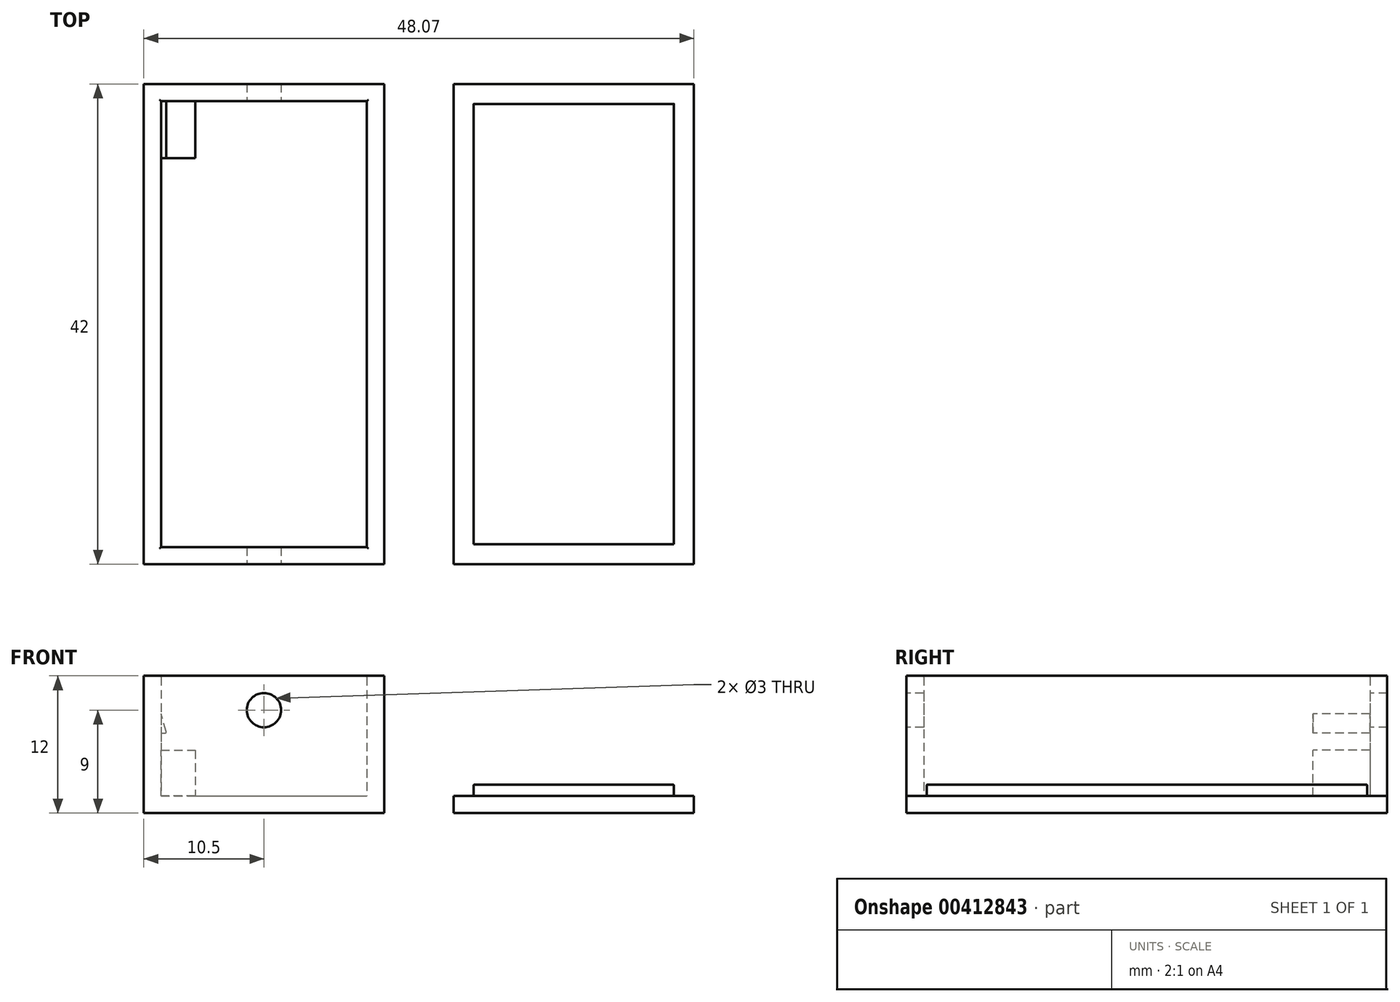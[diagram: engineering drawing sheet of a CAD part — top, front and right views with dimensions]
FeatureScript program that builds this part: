
annotation { "Feature Type Name" : "Feature", "Feature Type Description" : "" }
export const myFeature = defineFeature(function(context is Context, id is Id, definition is map)
    precondition{}
    {
        {
            var Q0;
            Q0=qCreatedBy(makeId("Top.planeOp"),FACE);
            var sketch = newSketch(context, id + "F0", { "sketchPlane" : qUnion([Q0])});
            skLineSegment(sketch, "E0.bottom", {"start": v(-10.5, 21) * mm, "end": v(10.5, 21) * mm});
            skLineSegment(sketch, "E0.top", {"start": v(-10.5, -21) * mm, "end": v(10.5, -21) * mm});
            skLineSegment(sketch, "E0.left", {"start": v(-10.5, 21) * mm, "end": v(-10.5, -21) * mm});
            skLineSegment(sketch, "E0.right", {"start": v(10.5, 21) * mm, "end": v(10.5, -21) * mm});
            skSolve(sketch);
        }
        {
            var Q0;
            Q0 = qSketchRegion(id + "F0", true);
            extrude(context, id + "F1", {"entities" : qUnion([Q0]), "depth" : 12 * mm});
        }
        {
            var Q0;
            Q0=makeQuery(id+"F1.opExtrude","CAP_FACE",FACE,{"disambiguationData":[OSD([sQuery(id+"F0.wireOp",EDGE,"E0.bottom"),sQuery(id+"F0.wireOp",EDGE,"E0.top"),sQuery(id+"F0.wireOp",EDGE,"E0.left"),sQuery(id+"F0.wireOp",EDGE,"E0.right")])],"isStart":false});
            shell(context, id + "F2", {"entities" : qUnion([Q0]), "thickness" : 1.5 * mm});
        }
        {
            var Q0;
            Q0=qCreatedBy(makeId("Top.planeOp"),FACE);
            var sketch = newSketch(context, id + "F3", { "sketchPlane" : qUnion([Q0])});
            skLineSegment(sketch, "E1.bottom", {"start": v(-10.5, 21) * mm, "end": v(-6, 21) * mm});
            skLineSegment(sketch, "E1.top", {"start": v(-10.5, 14.5) * mm, "end": v(-6, 14.5) * mm});
            skLineSegment(sketch, "E1.left", {"start": v(-10.5, 21) * mm, "end": v(-10.5, 14.5) * mm});
            skLineSegment(sketch, "E1.right", {"start": v(-6, 21) * mm, "end": v(-6, 14.5) * mm});
            skSolve(sketch);
        }
        {
            var Q0;
            Q0 = qSketchRegion(id + "F3", true);
            extrude(context, id + "F4", {"entities" : qUnion([Q0]), "operationType" : NewBodyOperationType.ADD, "depth" : (4 + 1.5) * mm});
        }
        {
            var Q0;
            Q0=makeQuery(id+"F4.opExtrude","CAP_FACE",FACE,{"disambiguationData":[OSD([sQuery(id+"F3.wireOp",EDGE,"E1.bottom"),sQuery(id+"F3.wireOp",EDGE,"E1.top"),sQuery(id+"F3.wireOp",EDGE,"E1.left"),sQuery(id+"F3.wireOp",EDGE,"E1.right")])],"isStart":false});
            cPlane(context, id + "F5", {"entities" : qUnion([Q0]), "cplaneType" : CPlaneType.OFFSET, "offset" : 1.5 * mm, "width" : 150 * mm, "height" : 150 * mm});
        }
        {
            var Q0;
            Q0=makeQuery(id+"F4.opExtrude","SWEPT_FACE",FACE,{"disambiguationData":[OSD([sQuery(id+"F3.wireOp",EDGE,"E1.top")])]});
            var sketch = newSketch(context, id + "F6", { "sketchPlane" : qUnion([Q0])});
            skLineSegment(sketch, "E2.0", {"start": v(-9, 12) * mm, "end": v(-9, 1.5) * mm, "construction": true});
            skLineSegment(sketch, "E3.0", {"start": v(-9, 5.5) * mm, "end": v(-6, 5.5) * mm, "construction": true});
            skLineSegment(sketch, "E4", {"start": v(-9, 7) * mm, "end": v(-8.5, 7) * mm});
            skLineSegment(sketch, "E5", {"start": v(-8.5, 7) * mm, "end": v(-9, 8.7) * mm});
            skLineSegment(sketch, "E6", {"start": v(-9, 8.7) * mm, "end": v(-9, 7) * mm});
            skSolve(sketch);
        }
        {
            var Q0;
            Q0 = qSketchRegion(id + "F6", true);
            extrude(context, id + "F7", {"entities" : qUnion([Q0]), "operationType" : NewBodyOperationType.ADD, "endBound" : BoundingType.UP_TO_NEXT, "oppositeDirection" : true, "depth" : 25 * mm});
        }
        {
            var Q0;
            Q0=makeQuery(id+"F1.opExtrude","SWEPT_FACE",FACE,{"disambiguationData":[OSD([sQuery(id+"F0.wireOp",EDGE,"E0.top")])]});
            var sketch = newSketch(context, id + "F8", { "sketchPlane" : qUnion([Q0])});
            skPoint(sketch, "E7", {"position": v(0, 9) * mm});
            skSolve(sketch);
        }
        {
            var Q0;
            Q0=sQuery(id+"F8.wireOp",VERTEX,"E7");
            var Q1;
            Q1=makeQuery(id+"F1.opExtrude","SWEPT_BODY",BODY,{"disambiguationData":[OSD([sQuery(id+"F0.wireOp",EDGE,"E0.bottom"),sQuery(id+"F0.wireOp",EDGE,"E0.top"),sQuery(id+"F0.wireOp",EDGE,"E0.left"),sQuery(id+"F0.wireOp",EDGE,"E0.right")])]});
            hole(context, id + "F9", {"style" : HoleStyle.SIMPLE, "endStyle" : HoleEndStyle.THROUGH, "holeDiameter" : 3 * mm, "isTappedThrough" : true, "tappedDepth" : 38.4 * mm, "tapClearance" : 3, "locations" : qUnion([Q0]), "scope" : qUnion([Q1])});
        }
        {
            var Q0;
            Q0=qCreatedBy(makeId("Top.planeOp"),FACE);
            var sketch = newSketch(context, id + "F10", { "sketchPlane" : qUnion([Q0])});
            skLineSegment(sketch, "E8.bottom", {"start": v(16.57, 21) * mm, "end": v(37.57, 21) * mm});
            skLineSegment(sketch, "E8.top", {"start": v(16.57, -21) * mm, "end": v(37.57, -21) * mm});
            skLineSegment(sketch, "E8.left", {"start": v(16.57, 21) * mm, "end": v(16.57, -21) * mm});
            skLineSegment(sketch, "E8.right", {"start": v(37.57, 21) * mm, "end": v(37.57, -21) * mm});
            skSolve(sketch);
        }
        {
            var Q0;
            Q0 = qSketchRegion(id + "F10", true);
            extrude(context, id + "F11", {"entities" : qUnion([Q0]), "depth" : 1.5 * mm});
        }
        {
            var Q0;
            Q0=makeQuery(id+"F11.opExtrude","CAP_FACE",FACE,{"disambiguationData":[OSD([sQuery(id+"F10.wireOp",EDGE,"E8.bottom"),sQuery(id+"F10.wireOp",EDGE,"E8.top"),sQuery(id+"F10.wireOp",EDGE,"E8.left"),sQuery(id+"F10.wireOp",EDGE,"E8.right")])],"isStart":false});
            var sketch = newSketch(context, id + "F12", { "sketchPlane" : qUnion([Q0])});
            skLineSegment(sketch, "E9.0", {"start": v(18.32, 19.25) * mm, "end": v(18.32, -19.25) * mm});
            skLineSegment(sketch, "E9.1", {"start": v(35.82, 19.25) * mm, "end": v(18.32, 19.25) * mm});
            skLineSegment(sketch, "E9.2", {"start": v(35.82, -19.25) * mm, "end": v(35.82, 19.25) * mm});
            skLineSegment(sketch, "E9.3", {"start": v(18.32, -19.25) * mm, "end": v(35.82, -19.25) * mm});
            skSolve(sketch);
        }
        {
            var Q0;
            Q0 = qSketchRegion(id + "F12", true);
            extrude(context, id + "F13", {"entities" : qUnion([Q0]), "operationType" : NewBodyOperationType.ADD, "depth" : 1 * mm});
        }
        {
            var Q0;
            Q0=makeQuery(id+"F7.opExtrude","SWEPT_EDGE",EDGE,{"disambiguationData":[OSD([sQuery(id+"F6.wireOp",EDGE,"E4"),sQuery(id+"F6.wireOp",EDGE,"E5")])]});
            var Q1;
            Q1=makeQuery(id+"FquBWeVs15Syh5w_1.1.F7.opExtrude","SWEPT_EDGE",EDGE,{"disambiguationData":[OSD([sQuery(id+"F6.wireOp",EDGE,"E4"),sQuery(id+"F6.wireOp",EDGE,"E5")])]});
            var Q2;
            Q2=makeQuery(id+"FKINZ1LQguasr2N_1.1.F7.opExtrude","SWEPT_EDGE",EDGE,{"disambiguationData":[OSD([sQuery(id+"F6.wireOp",EDGE,"E4"),sQuery(id+"F6.wireOp",EDGE,"E5")])]});
            var Q3;
            Q3=makeQuery(id+"FquBWeVs15Syh5w_1.1.FKINZ1LQguasr2N_1.1.F7.opExtrude","SWEPT_EDGE",EDGE,{"disambiguationData":[OSD([sQuery(id+"F6.wireOp",EDGE,"E4"),sQuery(id+"F6.wireOp",EDGE,"E5")])]});
            var Q4;
            Q4=makeQuery(id+"FquBWeVs15Syh5w_1.1.FKINZ1LQguasr2N_1.1.F7.opExtrude","SWEPT_EDGE",EDGE,{"disambiguationData":[OSD([sQuery(id+"F6.wireOp",EDGE,"E4"),sQuery(id+"F6.wireOp",EDGE,"E6")])]});
            var Q5;
            Q5=makeQuery(id+"FKINZ1LQguasr2N_1.1.F7.opExtrude","SWEPT_EDGE",EDGE,{"disambiguationData":[OSD([sQuery(id+"F6.wireOp",EDGE,"E4"),sQuery(id+"F6.wireOp",EDGE,"E6")])]});
            var Q6;
            Q6=makeQuery(id+"F7.opExtrude","SWEPT_EDGE",EDGE,{"disambiguationData":[OSD([sQuery(id+"F6.wireOp",EDGE,"E4"),sQuery(id+"F6.wireOp",EDGE,"E6")])]});
            var Q7;
            Q7=makeQuery(id+"FquBWeVs15Syh5w_1.1.F7.opExtrude","SWEPT_EDGE",EDGE,{"disambiguationData":[OSD([sQuery(id+"F6.wireOp",EDGE,"E4"),sQuery(id+"F6.wireOp",EDGE,"E6")])]});
            var Q8;
            Q8=makeQuery(id+"F13.opExtrude","CAP_EDGE",EDGE,{"disambiguationData":[OSD([sQuery(id+"F12.wireOp",EDGE,"E9.3")])],"isStart":false});
            var Q9;
            Q9=makeQuery(id+"F13.opExtrude","CAP_EDGE",EDGE,{"disambiguationData":[OSD([sQuery(id+"F12.wireOp",EDGE,"E9.2")])],"isStart":false});
            var Q10;
            Q10=makeQuery(id+"F13.opExtrude","CAP_EDGE",EDGE,{"disambiguationData":[OSD([sQuery(id+"F12.wireOp",EDGE,"E9.1")])],"isStart":false});
            var Q11;
            Q11=makeQuery(id+"F13.opExtrude","CAP_EDGE",EDGE,{"disambiguationData":[OSD([sQuery(id+"F12.wireOp",EDGE,"E9.0")])],"isStart":false});
            var Q12;
            {var subQ0=sQuery(id+"F0.wireOp",EDGE,"E0.left");Q12=makeQuery(id+"F2.opShell","OFFSET_EDGE",EDGE,{"disambiguationData":[OSD([subQ0]),TDD([makeQuery(id+"F1.opExtrude","CAP_EDGE",EDGE,{"disambiguationData":[OSD([subQ0])],"isStart":false})])]});}
            var Q13;
            {var subQ0=sQuery(id+"F0.wireOp",EDGE,"E0.top");Q13=makeQuery(id+"F2.opShell","OFFSET_EDGE",EDGE,{"disambiguationData":[OSD([subQ0]),TDD([makeQuery(id+"F1.opExtrude","CAP_EDGE",EDGE,{"disambiguationData":[OSD([subQ0])],"isStart":false})])]});}
            var Q14;
            {var subQ0=sQuery(id+"F0.wireOp",EDGE,"E0.right");Q14=makeQuery(id+"F2.opShell","OFFSET_EDGE",EDGE,{"disambiguationData":[OSD([subQ0]),TDD([makeQuery(id+"F1.opExtrude","CAP_EDGE",EDGE,{"disambiguationData":[OSD([subQ0])],"isStart":false})])]});}
            var Q15;
            {var subQ0=sQuery(id+"F0.wireOp",EDGE,"E0.bottom");Q15=makeQuery(id+"F2.opShell","OFFSET_EDGE",EDGE,{"disambiguationData":[OSD([subQ0]),TDD([makeQuery(id+"F1.opExtrude","CAP_EDGE",EDGE,{"disambiguationData":[OSD([subQ0])],"isStart":false})])]});}
            var Q16;
            Q16=makeQuery(id+"F9.hole-0.boolean.opBoolean","INTERSECT",EDGE,{"derivedFrom":[makeQuery(id+"F2.opShell","OFFSET_FACE",FACE,{"disambiguationData":[OSD([sQuery(id+"F0.wireOp",EDGE,"E0.bottom")])]}),makeQuery(id+"F9.hole-0.opRevolve","SWEPT_FACE",FACE,{"disambiguationData":[OSD([sQuery(id+"F9.hole-0.sketch.wireOp",EDGE,"core_line_2")])]})]});
            var Q17;
            Q17=makeQuery(id+"F9.hole-0.boolean.opBoolean","INTERSECT",EDGE,{"derivedFrom":[makeQuery(id+"F1.opExtrude","SWEPT_FACE",FACE,{"disambiguationData":[OSD([sQuery(id+"F0.wireOp",EDGE,"E0.bottom")])]}),makeQuery(id+"F9.hole-0.opRevolve","SWEPT_FACE",FACE,{"disambiguationData":[OSD([sQuery(id+"F9.hole-0.sketch.wireOp",EDGE,"core_line_2")])]})]});
            var Q18;
            Q18=makeQuery(id+"F9.hole-0.boolean.opBoolean","COPY",EDGE,{"derivedFrom":makeQuery(id+"F9.hole-0.opRevolve","SWEPT_EDGE",EDGE,{"disambiguationData":[OSD([sQuery(id+"F9.hole-0.sketch.wireOp",EDGE,"core_line_2"),sQuery(id+"F9.hole-0.sketch.wireOp",EDGE,"core_line_3")])]})});
            var Q19;
            Q19=makeQuery(id+"F9.hole-0.boolean.opBoolean","INTERSECT",EDGE,{"derivedFrom":[makeQuery(id+"F2.opShell","OFFSET_FACE",FACE,{"disambiguationData":[OSD([sQuery(id+"F0.wireOp",EDGE,"E0.top")])]}),makeQuery(id+"F9.hole-0.opRevolve","SWEPT_FACE",FACE,{"disambiguationData":[OSD([sQuery(id+"F9.hole-0.sketch.wireOp",EDGE,"core_line_2")])]})]});
            fillet(context, id + "F14", {"entities" : qUnion([Q0, Q1, Q2, Q3, Q4, Q5, Q6, Q7, Q8, Q9, Q10, Q11, Q12, Q13, Q14, Q15, Q16, Q17, Q18, Q19]), "radius" : .1 * mm, "tangentPropagation" : true, "allowEdgeOverflow" : false});
        }
    });
